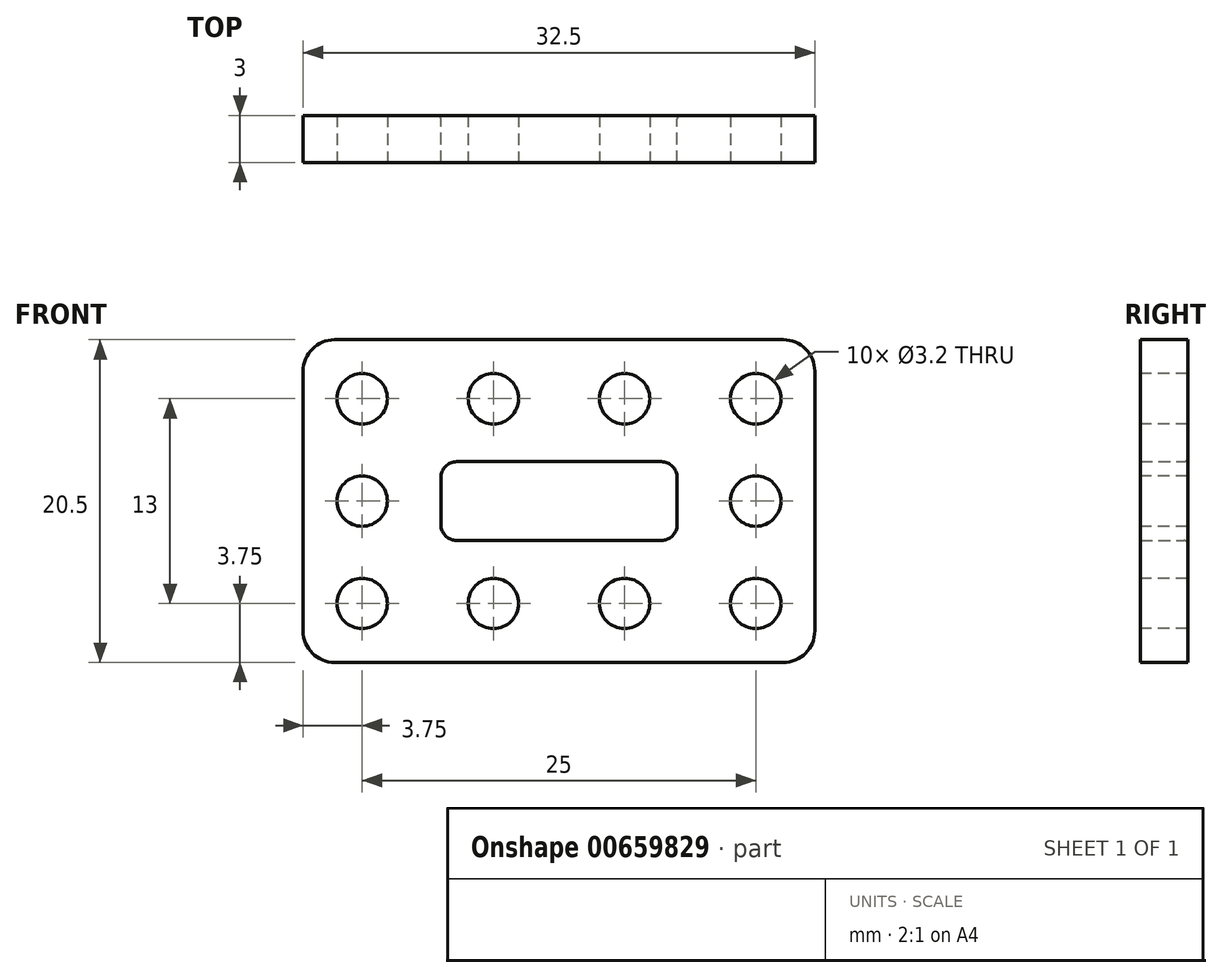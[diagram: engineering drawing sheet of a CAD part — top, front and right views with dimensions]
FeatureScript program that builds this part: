
annotation { "Feature Type Name" : "Feature", "Feature Type Description" : "" }
export const myFeature = defineFeature(function(context is Context, id is Id, definition is map)
    precondition{}
    {
        {
            var Q0;
            Q0=qCreatedBy(makeId("Front.planeOp"),FACE);
            var sketch = newSketch(context, id + "F0", { "sketchPlane" : qUnion([Q0])});
            skLineSegment(sketch, "E0.bottom", {"start": v(0, 0) * mm, "end": v(32.5, 0) * mm});
            skLineSegment(sketch, "E0.top", {"start": v(0, 20.5) * mm, "end": v(32.5, 20.5) * mm});
            skLineSegment(sketch, "E0.left", {"start": v(0, 0) * mm, "end": v(0, 20.5) * mm});
            skLineSegment(sketch, "E0.right", {"start": v(32.5, 0) * mm, "end": v(32.5, 20.5) * mm});
            skLineSegment(sketch, "E1.bottom", {"start": v(8.75, 12.75) * mm, "end": v(23.75, 12.75) * mm});
            skLineSegment(sketch, "E1.top", {"start": v(8.75, 7.75) * mm, "end": v(23.75, 7.75) * mm});
            skLineSegment(sketch, "E1.left", {"start": v(8.75, 12.75) * mm, "end": v(8.75, 7.75) * mm});
            skLineSegment(sketch, "E1.right", {"start": v(23.75, 12.75) * mm, "end": v(23.75, 7.75) * mm});
            skSolve(sketch);
        }
        {
            var Q0;
            Q0 = qSketchRegion(id + "F0", true);
            extrude(context, id + "F1", {"entities" : qUnion([Q0]), "depth" : 3 * mm, "offsetDistance" : 25 * mm});
        }
        {
            var Q0;
            Q0=makeQuery(id+"F1.opExtrude","CAP_FACE",FACE,{"disambiguationData":[OSD([sQuery(id+"F0.wireOp",EDGE,"E0.bottom"),sQuery(id+"F0.wireOp",EDGE,"E0.top"),sQuery(id+"F0.wireOp",EDGE,"E0.left"),sQuery(id+"F0.wireOp",EDGE,"E0.right"),sQuery(id+"F0.wireOp",EDGE,"E1.bottom"),sQuery(id+"F0.wireOp",EDGE,"E1.top"),sQuery(id+"F0.wireOp",EDGE,"E1.left"),sQuery(id+"F0.wireOp",EDGE,"E1.right")])],"isStart":false});
            var sketch = newSketch(context, id + "F2", { "sketchPlane" : qUnion([Q0])});
            skCircle(sketch, "E2", {"center": v(3.75, 16.75) * mm, "radius": 1.6 * mm});
            skCircle(sketch, "E3.0.1.0", {"center": v(3.75, 10.25) * mm, "radius": 1.6 * mm});
            skCircle(sketch, "E3.0.2.0", {"center": v(3.75, 3.75) * mm, "radius": 1.6 * mm});
            skCircle(sketch, "E3.1.0.0", {"center": v(12.08, 16.75) * mm, "radius": 1.6 * mm});
            skCircle(sketch, "E3.1.1.0", {"center": v(12.08, 10.25) * mm, "radius": 1.6 * mm});
            skCircle(sketch, "E3.1.2.0", {"center": v(12.08, 3.75) * mm, "radius": 1.6 * mm});
            skCircle(sketch, "E3.2.0.0", {"center": v(20.42, 16.75) * mm, "radius": 1.6 * mm});
            skCircle(sketch, "E3.2.1.0", {"center": v(20.42, 10.25) * mm, "radius": 1.6 * mm});
            skCircle(sketch, "E3.2.2.0", {"center": v(20.42, 3.75) * mm, "radius": 1.6 * mm});
            skCircle(sketch, "E3.3.0.0", {"center": v(28.75, 16.75) * mm, "radius": 1.6 * mm});
            skCircle(sketch, "E3.3.1.0", {"center": v(28.75, 10.25) * mm, "radius": 1.6 * mm});
            skCircle(sketch, "E3.3.2.0", {"center": v(28.75, 3.75) * mm, "radius": 1.6 * mm});
            skLineSegment(sketch, "E3.direction1", {"start": v(3.75, 16.75) * mm, "end": v(11.05, 16.75) * mm, "construction": true});
            skLineSegment(sketch, "E3.direction2", {"start": v(3.75, 16.75) * mm, "end": v(3.75, 10.15) * mm, "construction": true});
            skSolve(sketch);
        }
        {
            var Q0;
            Q0 = qSketchRegion(id + "F2", true);
            extrude(context, id + "F3", {"entities" : qUnion([Q0]), "operationType" : NewBodyOperationType.REMOVE, "oppositeDirection" : true, "depth" : 25 * mm, "offsetDistance" : 25 * mm});
        }
        {
            var Q0;
            Q0=makeQuery(id+"F1.opExtrude","SWEPT_EDGE",EDGE,{"disambiguationData":[OSD([sQuery(id+"F0.wireOp",EDGE,"E1.top"),sQuery(id+"F0.wireOp",EDGE,"E1.left")])]});
            var Q1;
            Q1=makeQuery(id+"F1.opExtrude","SWEPT_EDGE",EDGE,{"disambiguationData":[OSD([sQuery(id+"F0.wireOp",EDGE,"E1.bottom"),sQuery(id+"F0.wireOp",EDGE,"E1.left")])]});
            var Q2;
            Q2=makeQuery(id+"F1.opExtrude","SWEPT_EDGE",EDGE,{"disambiguationData":[OSD([sQuery(id+"F0.wireOp",EDGE,"E1.bottom"),sQuery(id+"F0.wireOp",EDGE,"E1.right")])]});
            var Q3;
            Q3=makeQuery(id+"F1.opExtrude","SWEPT_EDGE",EDGE,{"disambiguationData":[OSD([sQuery(id+"F0.wireOp",EDGE,"E1.top"),sQuery(id+"F0.wireOp",EDGE,"E1.right")])]});
            fillet(context, id + "F4", {"entities" : qUnion([Q0, Q1, Q2, Q3]), "radius" : 1 * mm, "tangentPropagation" : true, "allowEdgeOverflow" : false});
        }
        {
            var Q0;
            Q0=makeQuery(id+"F1.opExtrude","CAP_EDGE",EDGE,{"disambiguationData":[OSD([sQuery(id+"F0.wireOp",EDGE,"E1.bottom")])],"isStart":true});
            var Q1;
            {var subQ0=sQuery(id+"F0.wireOp",EDGE,"E1.left");var subQ1=sQuery(id+"F0.wireOp",EDGE,"E1.bottom");Q1=makeQuery(id+"F4.opFillet","BLEND_EDGE",EDGE,{"blendedFrom":[makeQuery(id+"F1.opExtrude","SWEPT_EDGE",EDGE,{"disambiguationData":[OSD([subQ1,subQ0])]}),makeQuery(id+"F1.opExtrude","CAP_FACE",FACE,{"disambiguationData":[OSD([sQuery(id+"F0.wireOp",EDGE,"E0.bottom"),sQuery(id+"F0.wireOp",EDGE,"E0.top"),sQuery(id+"F0.wireOp",EDGE,"E0.left"),sQuery(id+"F0.wireOp",EDGE,"E0.right"),subQ1,sQuery(id+"F0.wireOp",EDGE,"E1.top"),subQ0,sQuery(id+"F0.wireOp",EDGE,"E1.right")])],"isStart":true})],"blendedInto":[makeQuery(id+"F1.opExtrude","CAP_FACE",FACE,{"disambiguationData":[OSD([sQuery(id+"F0.wireOp",EDGE,"E0.bottom"),sQuery(id+"F0.wireOp",EDGE,"E0.top"),sQuery(id+"F0.wireOp",EDGE,"E0.left"),sQuery(id+"F0.wireOp",EDGE,"E0.right"),subQ1,sQuery(id+"F0.wireOp",EDGE,"E1.top"),subQ0,sQuery(id+"F0.wireOp",EDGE,"E1.right")])],"isStart":true})]});}
            var Q2;
            Q2=makeQuery(id+"F1.opExtrude","CAP_EDGE",EDGE,{"disambiguationData":[OSD([sQuery(id+"F0.wireOp",EDGE,"E1.left")])],"isStart":true});
            var Q3;
            {var subQ0=sQuery(id+"F0.wireOp",EDGE,"E1.left");var subQ1=sQuery(id+"F0.wireOp",EDGE,"E1.top");Q3=makeQuery(id+"F4.opFillet","BLEND_EDGE",EDGE,{"blendedFrom":[makeQuery(id+"F1.opExtrude","SWEPT_EDGE",EDGE,{"disambiguationData":[OSD([subQ1,subQ0])]}),makeQuery(id+"F1.opExtrude","CAP_FACE",FACE,{"disambiguationData":[OSD([sQuery(id+"F0.wireOp",EDGE,"E0.bottom"),sQuery(id+"F0.wireOp",EDGE,"E0.top"),sQuery(id+"F0.wireOp",EDGE,"E0.left"),sQuery(id+"F0.wireOp",EDGE,"E0.right"),sQuery(id+"F0.wireOp",EDGE,"E1.bottom"),subQ1,subQ0,sQuery(id+"F0.wireOp",EDGE,"E1.right")])],"isStart":true})],"blendedInto":[makeQuery(id+"F1.opExtrude","CAP_FACE",FACE,{"disambiguationData":[OSD([sQuery(id+"F0.wireOp",EDGE,"E0.bottom"),sQuery(id+"F0.wireOp",EDGE,"E0.top"),sQuery(id+"F0.wireOp",EDGE,"E0.left"),sQuery(id+"F0.wireOp",EDGE,"E0.right"),sQuery(id+"F0.wireOp",EDGE,"E1.bottom"),subQ1,subQ0,sQuery(id+"F0.wireOp",EDGE,"E1.right")])],"isStart":true})]});}
            var Q4;
            Q4=makeQuery(id+"F1.opExtrude","CAP_EDGE",EDGE,{"disambiguationData":[OSD([sQuery(id+"F0.wireOp",EDGE,"E1.top")])],"isStart":true});
            var Q5;
            {var subQ0=sQuery(id+"F0.wireOp",EDGE,"E1.right");var subQ1=sQuery(id+"F0.wireOp",EDGE,"E1.top");Q5=makeQuery(id+"F4.opFillet","BLEND_EDGE",EDGE,{"blendedFrom":[makeQuery(id+"F1.opExtrude","SWEPT_EDGE",EDGE,{"disambiguationData":[OSD([subQ1,subQ0])]}),makeQuery(id+"F1.opExtrude","CAP_FACE",FACE,{"disambiguationData":[OSD([sQuery(id+"F0.wireOp",EDGE,"E0.bottom"),sQuery(id+"F0.wireOp",EDGE,"E0.top"),sQuery(id+"F0.wireOp",EDGE,"E0.left"),sQuery(id+"F0.wireOp",EDGE,"E0.right"),sQuery(id+"F0.wireOp",EDGE,"E1.bottom"),subQ1,sQuery(id+"F0.wireOp",EDGE,"E1.left"),subQ0])],"isStart":true})],"blendedInto":[makeQuery(id+"F1.opExtrude","CAP_FACE",FACE,{"disambiguationData":[OSD([sQuery(id+"F0.wireOp",EDGE,"E0.bottom"),sQuery(id+"F0.wireOp",EDGE,"E0.top"),sQuery(id+"F0.wireOp",EDGE,"E0.left"),sQuery(id+"F0.wireOp",EDGE,"E0.right"),sQuery(id+"F0.wireOp",EDGE,"E1.bottom"),subQ1,sQuery(id+"F0.wireOp",EDGE,"E1.left"),subQ0])],"isStart":true})]});}
            var Q6;
            Q6=makeQuery(id+"F1.opExtrude","CAP_EDGE",EDGE,{"disambiguationData":[OSD([sQuery(id+"F0.wireOp",EDGE,"E1.right")])],"isStart":true});
            var Q7;
            {var subQ0=sQuery(id+"F0.wireOp",EDGE,"E1.right");var subQ1=sQuery(id+"F0.wireOp",EDGE,"E1.bottom");Q7=makeQuery(id+"F4.opFillet","BLEND_EDGE",EDGE,{"blendedFrom":[makeQuery(id+"F1.opExtrude","SWEPT_EDGE",EDGE,{"disambiguationData":[OSD([subQ1,subQ0])]}),makeQuery(id+"F1.opExtrude","CAP_FACE",FACE,{"disambiguationData":[OSD([sQuery(id+"F0.wireOp",EDGE,"E0.bottom"),sQuery(id+"F0.wireOp",EDGE,"E0.top"),sQuery(id+"F0.wireOp",EDGE,"E0.left"),sQuery(id+"F0.wireOp",EDGE,"E0.right"),subQ1,sQuery(id+"F0.wireOp",EDGE,"E1.top"),sQuery(id+"F0.wireOp",EDGE,"E1.left"),subQ0])],"isStart":true})],"blendedInto":[makeQuery(id+"F1.opExtrude","CAP_FACE",FACE,{"disambiguationData":[OSD([sQuery(id+"F0.wireOp",EDGE,"E0.bottom"),sQuery(id+"F0.wireOp",EDGE,"E0.top"),sQuery(id+"F0.wireOp",EDGE,"E0.left"),sQuery(id+"F0.wireOp",EDGE,"E0.right"),subQ1,sQuery(id+"F0.wireOp",EDGE,"E1.top"),sQuery(id+"F0.wireOp",EDGE,"E1.left"),subQ0])],"isStart":true})]});}
            fillet(context, id + "F5", {"entities" : qUnion([Q0, Q1, Q2, Q3, Q4, Q5, Q6, Q7]), "radius" : .25 * mm, "tangentPropagation" : true, "allowEdgeOverflow" : false});
        }
        {
            var Q0;
            Q0=makeQuery(id+"F1.opExtrude","SWEPT_EDGE",EDGE,{"disambiguationData":[OSD([sQuery(id+"F0.wireOp",EDGE,"E0.top"),sQuery(id+"F0.wireOp",EDGE,"E0.right")])]});
            var Q1;
            Q1=makeQuery(id+"F1.opExtrude","SWEPT_EDGE",EDGE,{"disambiguationData":[OSD([sQuery(id+"F0.wireOp",EDGE,"E0.bottom"),sQuery(id+"F0.wireOp",EDGE,"E0.right")])]});
            var Q2;
            Q2=makeQuery(id+"F1.opExtrude","SWEPT_EDGE",EDGE,{"disambiguationData":[OSD([sQuery(id+"F0.wireOp",EDGE,"E0.bottom"),sQuery(id+"F0.wireOp",EDGE,"E0.left")])]});
            var Q3;
            Q3=makeQuery(id+"F1.opExtrude","SWEPT_EDGE",EDGE,{"disambiguationData":[OSD([sQuery(id+"F0.wireOp",EDGE,"E0.top"),sQuery(id+"F0.wireOp",EDGE,"E0.left")])]});
            fillet(context, id + "F6", {"entities" : qUnion([Q0, Q1, Q2, Q3]), "radius" : 2 * mm, "tangentPropagation" : true, "allowEdgeOverflow" : false});
        }
    });
